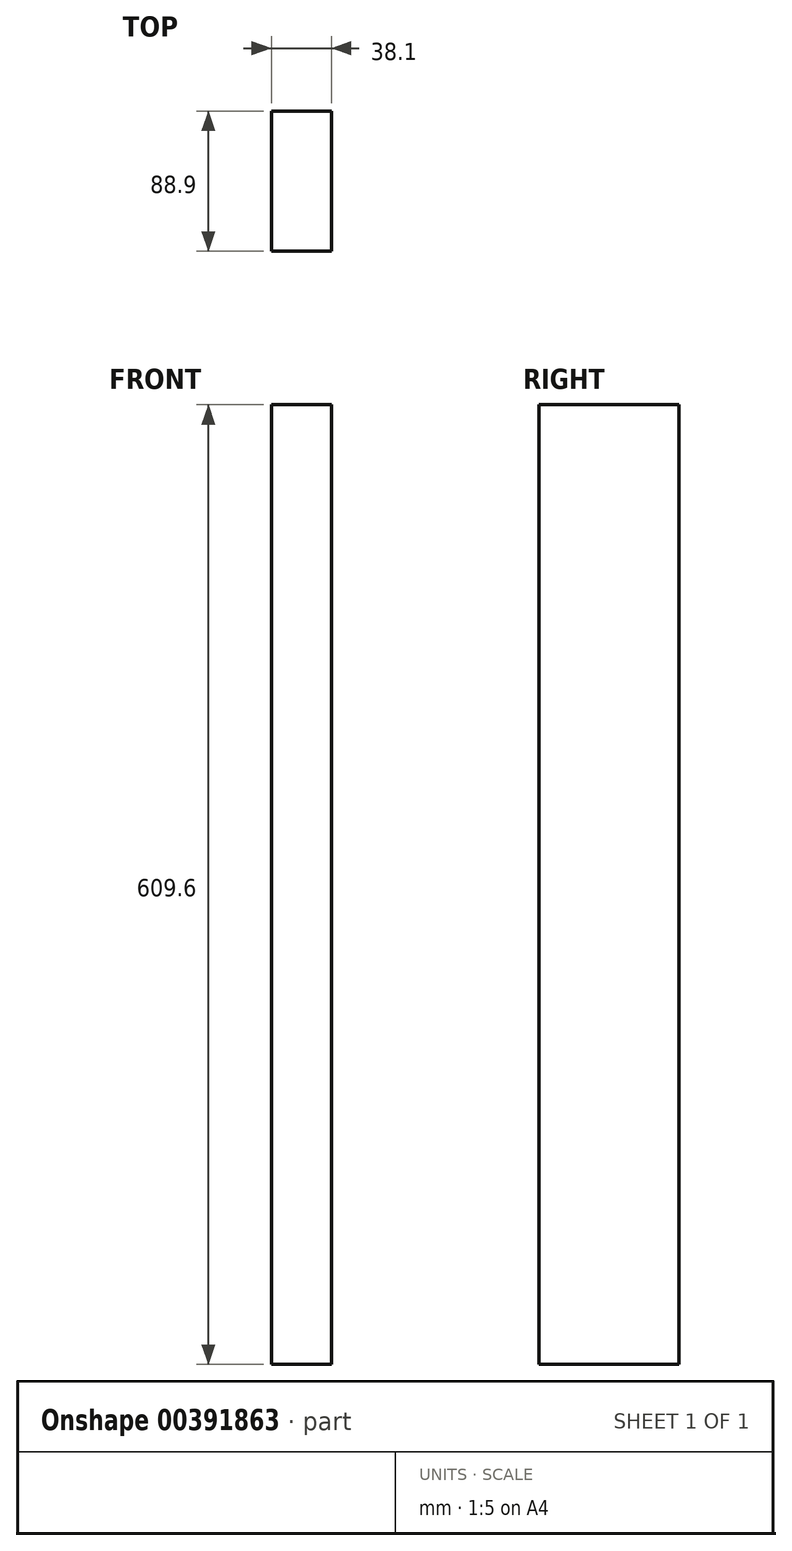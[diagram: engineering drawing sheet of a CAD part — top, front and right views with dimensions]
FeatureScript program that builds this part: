
annotation { "Feature Type Name" : "Feature", "Feature Type Description" : "" }
export const myFeature = defineFeature(function(context is Context, id is Id, definition is map)
    precondition{}
    {
        {
            var Q0;
            Q0=qCreatedBy(makeId("Top.planeOp"),FACE);
            var sketch = newSketch(context, id + "F0", { "sketchPlane" : qUnion([Q0])});
            skLineSegment(sketch, "E0.bottom", {"start": v(0, 0) * mm, "end": v(38.1, 0) * mm});
            skLineSegment(sketch, "E0.top", {"start": v(0, -88.9) * mm, "end": v(38.1, -88.9) * mm});
            skLineSegment(sketch, "E0.left", {"start": v(0, 0) * mm, "end": v(0, -88.9) * mm});
            skLineSegment(sketch, "E0.right", {"start": v(38.1, 0) * mm, "end": v(38.1, -88.9) * mm});
            skSolve(sketch);
        }
        {
            var Q0;
            Q0=makeQuery(id+"F0.imprint","IMPRINT",FACE,{"disambiguationData":[TD([[makeQuery(id+"F0.imprint","IMPRINT",EDGE,{"derivedFrom":sQuery(id+"F0.wireOp",EDGE,"E0.bottom")}),-1.0]])]});
            extrude(context, id + "F1", {"entities" : qUnion([Q0]), "endBound" : BoundingType.SYMMETRIC, "depth" : 609.6 * mm});
        }
    });
